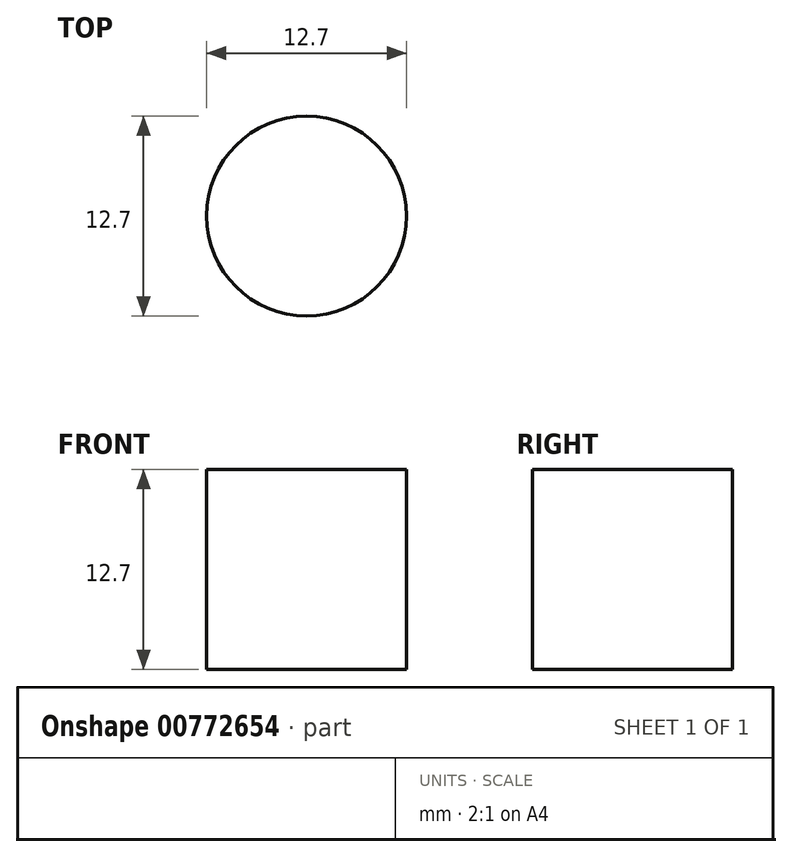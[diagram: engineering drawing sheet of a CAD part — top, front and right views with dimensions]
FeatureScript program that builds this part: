
annotation { "Feature Type Name" : "Feature", "Feature Type Description" : "" }
export const myFeature = defineFeature(function(context is Context, id is Id, definition is map)
    precondition{}
    {
        {
            var Q0;
            Q0=qCreatedBy(makeId("Front.planeOp"),FACE);
            var sketch = newSketch(context, id + "F0", { "sketchPlane" : qUnion([Q0])});
            skLineSegment(sketch, "E0", {"start": v(0, 0) * mm, "end": v(-6.35, 0) * mm});
            skLineSegment(sketch, "E1", {"start": v(-6.35, 0) * mm, "end": v(-6.35, 12.7) * mm});
            skLineSegment(sketch, "E2", {"start": v(-6.35, 12.7) * mm, "end": v(0, 12.7) * mm});
            skLineSegment(sketch, "E3", {"start": v(0, 12.7) * mm, "end": v(0, 0) * mm});
            skSolve(sketch);
        }
        {
            var Q0;
            Q0=makeQuery(id+"F0.imprint","IMPRINT",FACE,{"disambiguationData":[TD([[makeQuery(id+"F0.imprint","IMPRINT",EDGE,{"derivedFrom":sQuery(id+"F0.wireOp",EDGE,"E0")}),-1.0]])]});
            var Q1;
            Q1=sQuery(id+"F0.wireOp",EDGE,"E3");
            revolve(context, id + "F1", {"entities" : qUnion([Q0]), "axis" : qUnion([Q1]), "revolveType" : RevolveType.FULL});
        }
    });
